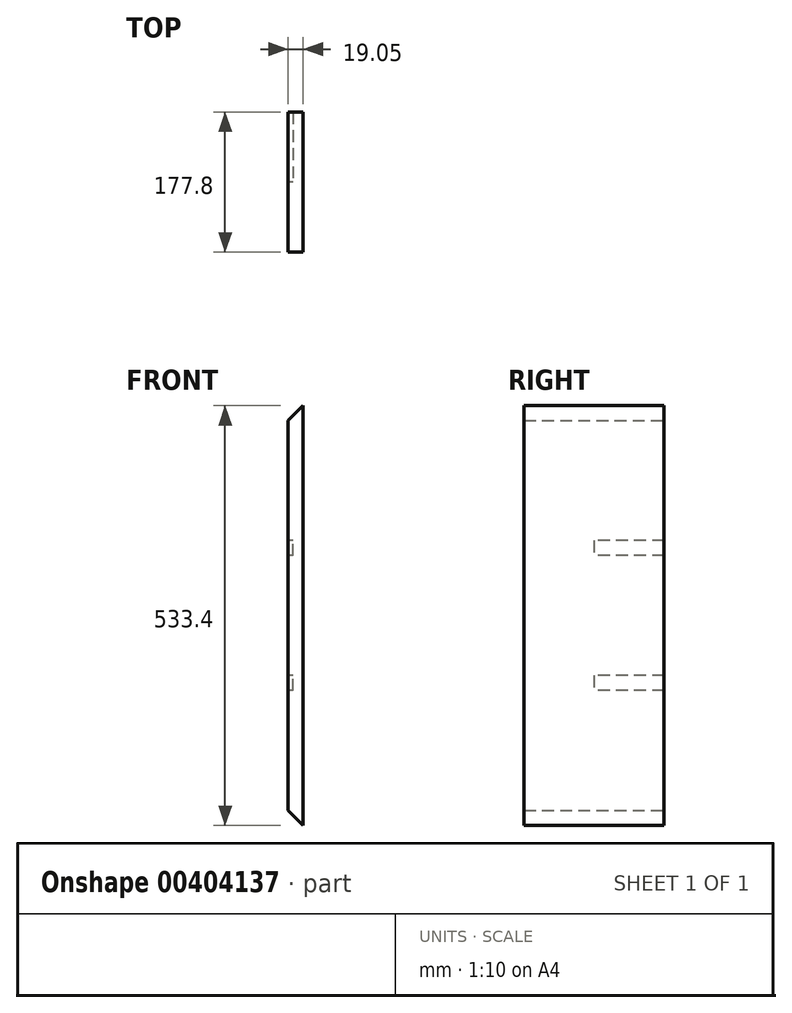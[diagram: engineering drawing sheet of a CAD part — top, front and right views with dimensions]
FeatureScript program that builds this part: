
annotation { "Feature Type Name" : "Feature", "Feature Type Description" : "" }
export const myFeature = defineFeature(function(context is Context, id is Id, definition is map)
    precondition{}
    {
        {
            var Q0;
            Q0=qCreatedBy(makeId("Front.planeOp"),FACE);
            var sketch = newSketch(context, id + "F0", { "sketchPlane" : qUnion([Q0])});
            skLineSegment(sketch, "E0.right", {"start": v(19.05, 19.05) * mm, "end": v(19.05, 514.35) * mm});
            skLineSegment(sketch, "E1.MirrorCS", {"start": v(38.1, 0) * mm, "end": v(38.1, 533.4) * mm});
            skLineSegment(sketch, "E2.MirrorCS", {"start": v(38.1, 0) * mm, "end": v(19.05, 19.05) * mm});
            skLineSegment(sketch, "E3.MirrorCS", {"start": v(38.1, 533.4) * mm, "end": v(19.05, 514.35) * mm});
            skPoint(sketch, "E4.start.orphan", {"position": v(0, 0) * mm});
            skSolve(sketch);
        }
        {
            var Q0;
            Q0 = qSketchRegion(id + "F0", true);
            extrude(context, id + "F1", {"entities" : qUnion([Q0]), "endBound" : BoundingType.SYMMETRIC, "depth" : 177.8 * mm});
        }
        {
            var Q0;
            Q0=makeQuery(id+"F1.opExtrude","SWEPT_FACE",FACE,{"disambiguationData":[OSD([sQuery(id+"F0.wireOp",EDGE,"E0.right")])]});
            var sketch = newSketch(context, id + "F2", { "sketchPlane" : qUnion([Q0])});
            skLineSegment(sketch, "E5.bottom", {"start": v(-88.9, 190.5) * mm, "end": v(0, 190.5) * mm});
            skLineSegment(sketch, "E5.top", {"start": v(-88.9, 171.45) * mm, "end": v(0, 171.45) * mm});
            skLineSegment(sketch, "E5.left", {"start": v(-88.9, 190.5) * mm, "end": v(-88.9, 171.45) * mm});
            skLineSegment(sketch, "E5.right", {"start": v(0, 190.5) * mm, "end": v(0, 171.45) * mm});
            skLineSegment(sketch, "E6.bottom", {"start": v(-88.9, 361.95) * mm, "end": v(0, 361.95) * mm});
            skLineSegment(sketch, "E6.top", {"start": v(-88.9, 342.9) * mm, "end": v(0, 342.9) * mm});
            skLineSegment(sketch, "E6.left", {"start": v(-88.9, 361.95) * mm, "end": v(-88.9, 342.9) * mm});
            skLineSegment(sketch, "E6.right", {"start": v(0, 361.95) * mm, "end": v(0, 342.9) * mm});
            skSolve(sketch);
        }
        {
            var Q0;
            Q0 = qSketchRegion(id + "F2", true);
            extrude(context, id + "F3", {"entities" : qUnion([Q0]), "operationType" : NewBodyOperationType.REMOVE, "oppositeDirection" : true, "depth" : 6.35 * mm});
        }
    });
